# Revit family: FU_Table_Sandler_Cono 4002 D36
name_source: partatom
category: Furniture
units: mm (PartAtom-declared; Revit-internal decimal feet)

## family parameters
Always vertical = No
Cut with Voids When Loaded = No
OmniClass Number = 23.21.23.15.17
Render Appearance Source = Family Geometry
Room Calculation Point = No
Shared = No
Work Plane-Based = Yes

## types (1)
- CONO 4002 - D36
    BIMobject category = Table
    BIMobject category code = furniture-table
    BIMobject main category = Furniture
    BIMobject main category code = furniture
    Base Material = Metal - M2 Lacquer - Pearl White RAL 1013
    Brand url = https://www.sandlerseating.com
    Default Elevation = 0 mm  [stored 0 ft]
    Depth = 600 mm  [stored 1.9685 ft]
    Description = Dining table with wider metal base and table top measuring 90cm/36" in diameter. 75cm/29.5" high. The round table top is available in woodgrain or a lacquered finish, with a reverse knife edge profile. Other profiles and materials available by special request.
    Edition number = 1
    Height = 720 mm  [stored 2.3622 ft]
    IFC Classification = Furnishing Element
    Manufacturer = Sandler
    Manufacturer country = USA
    Manufacturer name = Sandler
    Masterformat 2014 Code = 12 48 43.13
    Masterformat 2014 Description = Table Mats
    Model = CONO 4002 D36
    OmniClass Code = 23-21 23 15 17
    Product Guid = ??
    Product SKU = ??
    Product data url = https://www.sandlerseating.com
    Product family = Furniture
    Product group = Table
    Product name = CONO 4002
    Product url = https://www.sandlerseating.com
    QR code = https://www.sandlerseating.com
    Top Type = FU_Top_Sandler_EF125 : 125EF Top 90dia
    URL = https://www.sandlerseating.com
    Uniformat II Description = Movable Furnishings
    Width = 600 mm  [stored 1.9685 ft]

note: [stored X ft] marks values corroborated as IEEE doubles in the binary element streams (Revit-internal decimal feet)

## geometry (parser evidence)
native form markers: Sweep x8
no freeform markers — native parametric forms only
